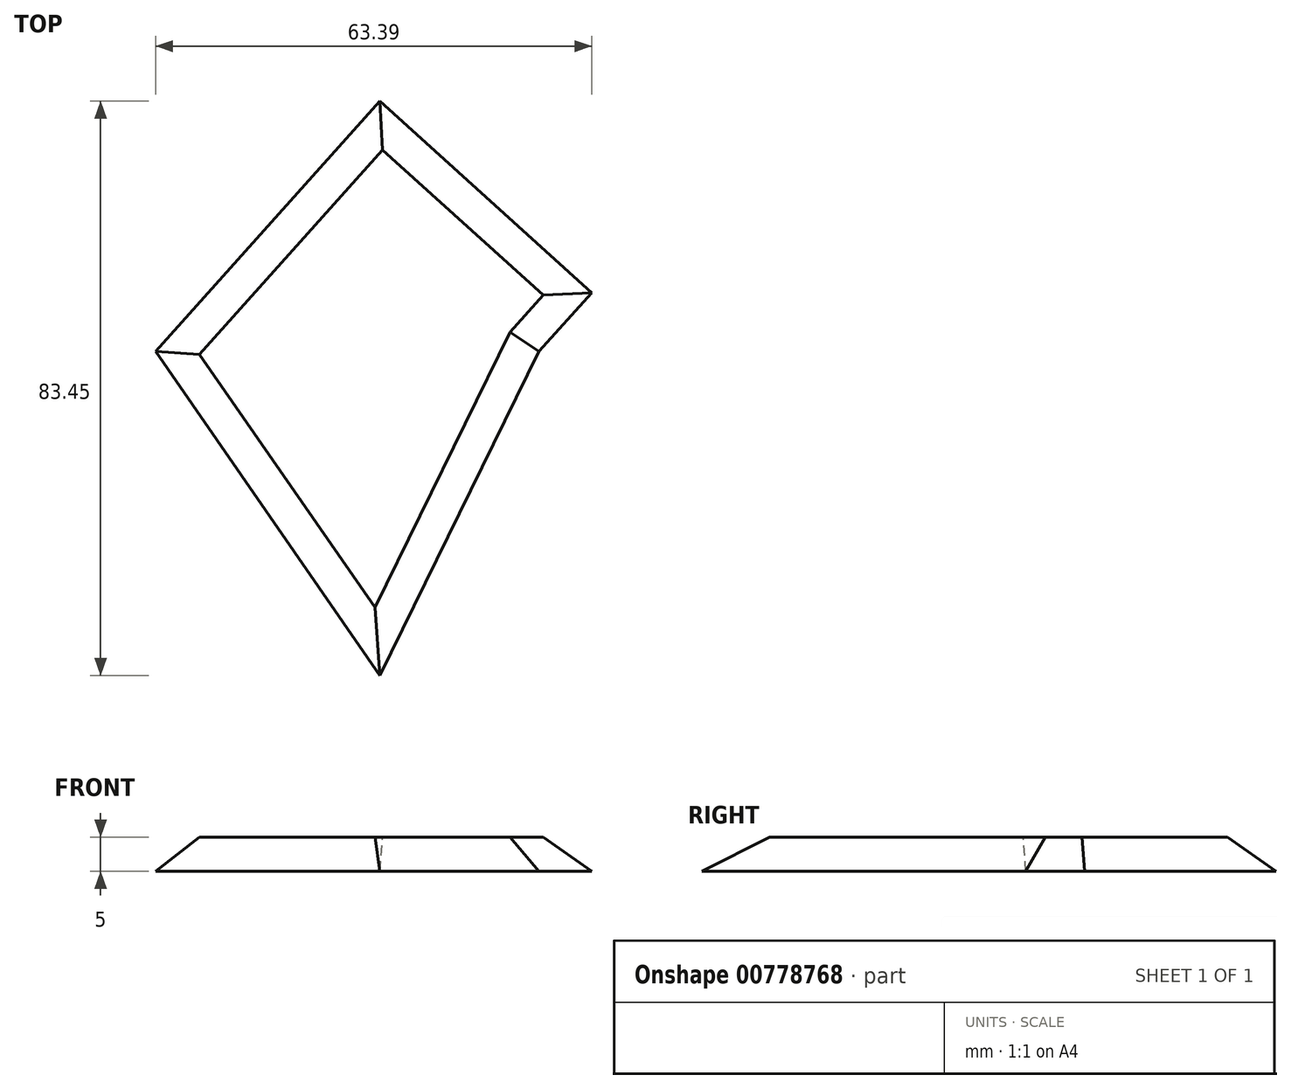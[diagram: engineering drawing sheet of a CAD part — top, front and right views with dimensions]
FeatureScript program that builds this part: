
annotation { "Feature Type Name" : "Feature", "Feature Type Description" : "" }
export const myFeature = defineFeature(function(context is Context, id is Id, definition is map)
    precondition{}
    {
        {
            var Q0;
            Q0=qCreatedBy(makeId("Top.planeOp"),FACE);
            var sketch = newSketch(context, id + "F0", { "sketchPlane" : qUnion([Q0])});
            skLineSegment(sketch, "E0", {"start": v(0, 48.94) * mm, "end": v(30.79, 21.1) * mm});
            skLineSegment(sketch, "E1", {"start": v(30.79, 21.1) * mm, "end": v(23.06, 12.55) * mm});
            skLineSegment(sketch, "E2", {"start": v(23.06, 12.55) * mm, "end": v(0, -34.51) * mm});
            skLineSegment(sketch, "E3", {"start": v(0, -34.51) * mm, "end": v(-32.6, 12.55) * mm});
            skLineSegment(sketch, "E4", {"start": v(-32.6, 12.55) * mm, "end": v(0, 48.94) * mm});
            skSolve(sketch);
        }
        {
            var Q0;
            Q0=makeQuery(id+"F0.imprint","IMPRINT",FACE,{"disambiguationData":[TD([[makeQuery(id+"F0.imprint","IMPRINT",EDGE,{"derivedFrom":sQuery(id+"F0.wireOp",EDGE,"E0")}),-1.0]])]});
            extrude(context, id + "F1", {"entities" : qUnion([Q0]), "depth" : 5 * mm, "offsetDistance" : 25 * mm});
        }
        {
            var Q0;
            Q0=makeQuery(id+"F1.opExtrude","CAP_EDGE",EDGE,{"disambiguationData":[OSD([sQuery(id+"F0.wireOp",EDGE,"E4")])],"isStart":false});
            var Q1;
            Q1=makeQuery(id+"F1.opExtrude","CAP_EDGE",EDGE,{"disambiguationData":[OSD([sQuery(id+"F0.wireOp",EDGE,"E3")])],"isStart":false});
            var Q2;
            Q2=makeQuery(id+"F1.opExtrude","CAP_EDGE",EDGE,{"disambiguationData":[OSD([sQuery(id+"F0.wireOp",EDGE,"E2")])],"isStart":false});
            var Q3;
            Q3=makeQuery(id+"F1.opExtrude","CAP_EDGE",EDGE,{"disambiguationData":[OSD([sQuery(id+"F0.wireOp",EDGE,"E1")])],"isStart":false});
            var Q4;
            Q4=makeQuery(id+"F1.opExtrude","CAP_EDGE",EDGE,{"disambiguationData":[OSD([sQuery(id+"F0.wireOp",EDGE,"E0")])],"isStart":false});
            chamfer(context, id + "F2", {"entities" : qUnion([Q0, Q1, Q2, Q3, Q4]), "width" : 5 * mm, "tangentPropagation" : true});
        }
    });
